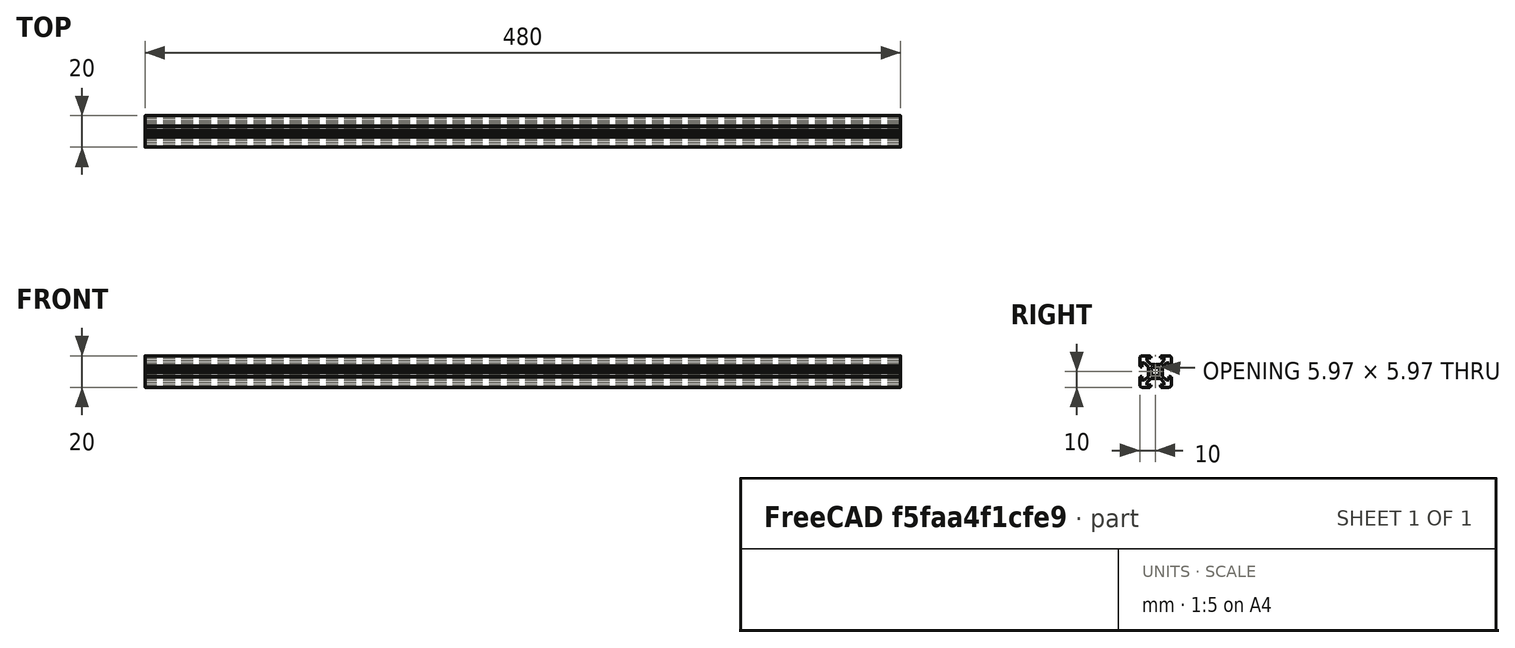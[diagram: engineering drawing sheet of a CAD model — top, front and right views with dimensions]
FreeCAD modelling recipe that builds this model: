
FCSTD DOCUMENT  (FreeCAD 0.19R)
Label: Tslot48
License: All rights reserved
LicenseURL: http://en.wikipedia.org/wiki/All_rights_reserved
objects: Sketcher::SketchObject×1, PartDesign::Pad×1, PartDesign::Body×1
note: 4 computed .brp shape members not serialized (recipe doc carries the construction recipe); baked Part::Feature solids carry a one-line shape summary decoded from their .brp

FEATURE [Sketcher::SketchObject] Sketch  label="T-Slot-Skizze"
  FullyConstrained = true
  MapMode = 5
  Placement = pos=(0,0,0) rot=(0.57735,0.57735,0.57735;2.0944rad)
  Support = -> [YZ_Plane]
  sketch-geometry (98):
    g0: LineSegment StartX=0 StartY=4.1 StartZ=0 EndX=0.65 EndY=4.5 EndZ=0
    g1: LineSegment StartX=0.65 StartY=4.5 StartZ=0 EndX=3 EndY=4.5 EndZ=0
    g2: LineSegment StartX=3 StartY=4.5 StartZ=0 EndX=5.5 EndY=7 EndZ=0
    g3: LineSegment StartX=5.5 StartY=7 StartZ=0 EndX=5.5 EndY=8.5 EndZ=0
    g4: LineSegment StartX=5.5 StartY=8.5 StartZ=0 EndX=3 EndY=8.5 EndZ=0
    g5: LineSegment StartX=3 StartY=8.5 StartZ=0 EndX=3 EndY=9.5 EndZ=0
    g6: LineSegment StartX=3 StartY=9.5 StartZ=0 EndX=3.5 EndY=9.5 EndZ=0
    g7: LineSegment StartX=3.5 StartY=9.5 StartZ=0 EndX=3.5 EndY=10 EndZ=0
    g8: LineSegment StartX=3.5 StartY=10 StartZ=0 EndX=8.5 EndY=10 EndZ=0
    g9: LineSegment StartX=10 StartY=8.5 StartZ=0 EndX=10 EndY=3.5 EndZ=0
    g10: LineSegment StartX=10 StartY=3.5 StartZ=0 EndX=9.5 EndY=3.5 EndZ=0
    g11: LineSegment StartX=9.5 StartY=3.5 StartZ=0 EndX=9.5 EndY=3 EndZ=0
    g12: LineSegment StartX=9.5 StartY=3 StartZ=0 EndX=8.5 EndY=3 EndZ=0
    g13: LineSegment StartX=8.5 StartY=3 StartZ=0 EndX=8.5 EndY=5.5 EndZ=0
    g14: LineSegment StartX=8.5 StartY=5.5 StartZ=0 EndX=7 EndY=5.5 EndZ=0
    g15: LineSegment StartX=7 StartY=5.5 StartZ=0 EndX=4.5 EndY=3 EndZ=0
    g16: LineSegment StartX=4.5 StartY=3 StartZ=0 EndX=4.5 EndY=0.65 EndZ=0
    g17: LineSegment StartX=4.5 StartY=0.65 StartZ=0 EndX=4.1 EndY=0 EndZ=0
    g18: ArcOfCircle CenterX=8.5 CenterY=8.5 CenterZ=0 NormalX=0 NormalY=0 NormalZ=1 AngleXU=0 Radius=1.5 StartAngle=0 EndAngle=1.5708
    g19: LineSegment StartX=0 StartY=-4.1 StartZ=0 EndX=0.65 EndY=-4.5 EndZ=0
    g20: LineSegment StartX=0.65 StartY=-4.5 StartZ=0 EndX=3 EndY=-4.5 EndZ=0
    g21: LineSegment StartX=3 StartY=-4.5 StartZ=0 EndX=5.5 EndY=-7 EndZ=0
    g22: LineSegment StartX=5.5 StartY=-7 StartZ=0 EndX=5.5 EndY=-8.5 EndZ=0
    g23: LineSegment StartX=5.5 StartY=-8.5 StartZ=0 EndX=3 EndY=-8.5 EndZ=0
    g24: LineSegment StartX=3 StartY=-8.5 StartZ=0 EndX=3 EndY=-9.5 EndZ=0
    g25: LineSegment StartX=3 StartY=-9.5 StartZ=0 EndX=3.5 EndY=-9.5 EndZ=0
    g26: LineSegment StartX=3.5 StartY=-9.5 StartZ=0 EndX=3.5 EndY=-10 EndZ=0
    g27: LineSegment StartX=3.5 StartY=-10 StartZ=0 EndX=8.5 EndY=-10 EndZ=0
    g28: LineSegment StartX=10 StartY=-8.5 StartZ=0 EndX=10 EndY=-3.5 EndZ=0
    g29: LineSegment StartX=10 StartY=-3.5 StartZ=0 EndX=9.5 EndY=-3.5 EndZ=0
    g30: LineSegment StartX=9.5 StartY=-3.5 StartZ=0 EndX=9.5 EndY=-3 EndZ=0
    g31: LineSegment StartX=9.5 StartY=-3 StartZ=0 EndX=8.5 EndY=-3 EndZ=0
    g32: LineSegment StartX=8.5 StartY=-3 StartZ=0 EndX=8.5 EndY=-5.5 EndZ=0
    g33: LineSegment StartX=8.5 StartY=-5.5 StartZ=0 EndX=7 EndY=-5.5 EndZ=0
    g34: LineSegment StartX=7 StartY=-5.5 StartZ=0 EndX=4.5 EndY=-3 EndZ=0
    g35: LineSegment StartX=4.5 StartY=-3 StartZ=0 EndX=4.5 EndY=-0.65 EndZ=0
    g36: ArcOfCircle CenterX=8.5 CenterY=-8.5 CenterZ=0 NormalX=0 NormalY=0 NormalZ=1 AngleXU=0 Radius=1.5 StartAngle=4.71239 EndAngle=6.28319
    g37: LineSegment StartX=4.5 StartY=-0.65 StartZ=0 EndX=4.1 EndY=0 EndZ=0
    g38: LineSegment StartX=0 StartY=-4.1 StartZ=0 EndX=-0.65 EndY=-4.5 EndZ=0
    g39: LineSegment StartX=-0.65 StartY=-4.5 StartZ=0 EndX=-3 EndY=-4.5 EndZ=0
    g40: LineSegment StartX=-3 StartY=-4.5 StartZ=0 EndX=-5.5 EndY=-7 EndZ=0
    g41: LineSegment StartX=-5.5 StartY=-7 StartZ=0 EndX=-5.5 EndY=-8.5 EndZ=0
    g42: LineSegment StartX=-5.5 StartY=-8.5 StartZ=0 EndX=-3 EndY=-8.5 EndZ=0
    g43: LineSegment StartX=-3 StartY=-8.5 StartZ=0 EndX=-3 EndY=-9.5 EndZ=0
    g44: LineSegment StartX=-3 StartY=-9.5 StartZ=0 EndX=-3.5 EndY=-9.5 EndZ=0
    g45: LineSegment StartX=-3.5 StartY=-9.5 StartZ=0 EndX=-3.5 EndY=-10 EndZ=0
    g46: LineSegment StartX=-3.5 StartY=-10 StartZ=0 EndX=-8.5 EndY=-10 EndZ=0
    g47: LineSegment StartX=-10 StartY=-8.5 StartZ=0 EndX=-10 EndY=-3.5 EndZ=0
    g48: LineSegment StartX=-10 StartY=-3.5 StartZ=0 EndX=-9.5 EndY=-3.5 EndZ=0
    g49: LineSegment StartX=-9.5 StartY=-3.5 StartZ=0 EndX=-9.5 EndY=-3 EndZ=0
    g50: LineSegment StartX=-9.5 StartY=-3 StartZ=0 EndX=-8.5 EndY=-3 EndZ=0
    g51: LineSegment StartX=-8.5 StartY=-3 StartZ=0 EndX=-8.5 EndY=-5.5 EndZ=0
    g52: LineSegment StartX=-8.5 StartY=-5.5 StartZ=0 EndX=-7 EndY=-5.5 EndZ=0
    g53: LineSegment StartX=-7 StartY=-5.5 StartZ=0 EndX=-4.5 EndY=-3 EndZ=0
    g54: LineSegment StartX=-4.5 StartY=-3 StartZ=0 EndX=-4.5 EndY=-0.65 EndZ=0
    g55: ArcOfCircle CenterX=-8.5 CenterY=-8.5 CenterZ=0 NormalX=0 NormalY=0 NormalZ=1 AngleXU=0 Radius=1.5 StartAngle=3.14159 EndAngle=4.71239
    g56: LineSegment StartX=-4.5 StartY=-0.65 StartZ=0 EndX=-4.1 EndY=0 EndZ=0
    g57: LineSegment StartX=-0.65 StartY=4.5 StartZ=0 EndX=-3 EndY=4.5 EndZ=0
    g58: LineSegment StartX=-3 StartY=4.5 StartZ=0 EndX=-5.5 EndY=7 EndZ=0
    g59: LineSegment StartX=-5.5 StartY=7 StartZ=0 EndX=-5.5 EndY=8.5 EndZ=0
    g60: LineSegment StartX=-5.5 StartY=8.5 StartZ=0 EndX=-3 EndY=8.5 EndZ=0
    g61: LineSegment StartX=-3 StartY=8.5 StartZ=0 EndX=-3 EndY=9.5 EndZ=0
    g62: LineSegment StartX=-3 StartY=9.5 StartZ=0 EndX=-3.5 EndY=9.5 EndZ=0
    g63: LineSegment StartX=-3.5 StartY=9.5 StartZ=0 EndX=-3.5 EndY=10 EndZ=0
    g64: LineSegment StartX=-3.5 StartY=10 StartZ=0 EndX=-8.5 EndY=10 EndZ=0
    g65: LineSegment StartX=-10 StartY=8.5 StartZ=0 EndX=-10 EndY=3.5 EndZ=0
    g66: LineSegment StartX=-10 StartY=3.5 StartZ=0 EndX=-9.5 EndY=3.5 EndZ=0
    g67: LineSegment StartX=-9.5 StartY=3.5 StartZ=0 EndX=-9.5 EndY=3 EndZ=0
    g68: LineSegment StartX=-9.5 StartY=3 StartZ=0 EndX=-8.5 EndY=3 EndZ=0
    g69: LineSegment StartX=-8.5 StartY=3 StartZ=0 EndX=-8.5 EndY=5.5 EndZ=0
    g70: LineSegment StartX=-8.5 StartY=5.5 StartZ=0 EndX=-7 EndY=5.5 EndZ=0
    g71: LineSegment StartX=-7 StartY=5.5 StartZ=0 EndX=-4.5 EndY=3 EndZ=0
    g72: LineSegment StartX=-4.5 StartY=3 StartZ=0 EndX=-4.5 EndY=0.65 EndZ=0
    g73: ArcOfCircle CenterX=-8.5 CenterY=8.5 CenterZ=0 NormalX=0 NormalY=0 NormalZ=1 AngleXU=0 Radius=1.5 StartAngle=1.5708 EndAngle=3.14159
    g74: LineSegment StartX=-4.5 StartY=0.65 StartZ=0 EndX=-4.1 EndY=0 EndZ=0
    g75: LineSegment StartX=0 StartY=4.1 StartZ=0 EndX=-0.65 EndY=4.5 EndZ=0
    g76: Circle CenterX=0 CenterY=0 CenterZ=0 NormalX=0 NormalY=0 NormalZ=1 AngleXU=0 Radius=3.55
    g77: Circle CenterX=0 CenterY=0 CenterZ=0 NormalX=0 NormalY=0 NormalZ=1 AngleXU=0 Radius=2.75
    g78: LineSegment StartX=1.3405 StartY=2.40116 StartZ=0 EndX=1.92324 EndY=2.9839 EndZ=0
    g79: LineSegment StartX=1.92324 StartY=2.9839 StartZ=0 EndX=2.9839 EndY=1.92324 EndZ=0
    g80: LineSegment StartX=2.9839 StartY=1.92324 StartZ=0 EndX=2.40116 EndY=1.3405 EndZ=0
    g81: ArcOfCircle CenterX=0 CenterY=0 CenterZ=0 NormalX=0 NormalY=0 NormalZ=1 AngleXU=0 Radius=2.75 StartAngle=0 EndAngle=0.509172
    g82: ArcOfCircle CenterX=0 CenterY=0 CenterZ=0 NormalX=0 NormalY=0 NormalZ=1 AngleXU=0 Radius=2.75 StartAngle=1.06162 EndAngle=1.5708
    g83: LineSegment StartX=-1.3405 StartY=2.40116 StartZ=0 EndX=-1.92324 EndY=2.9839 EndZ=0
    g84: LineSegment StartX=-1.92324 StartY=2.9839 StartZ=0 EndX=-2.9839 EndY=1.92324 EndZ=0
    g85: LineSegment StartX=-2.9839 StartY=1.92324 StartZ=0 EndX=-2.40116 EndY=1.3405 EndZ=0
    g86: ArcOfCircle CenterX=-1.3e-15 CenterY=6e-16 CenterZ=0 NormalX=0 NormalY=0 NormalZ=1 AngleXU=0 Radius=2.75 StartAngle=2.63242 EndAngle=3.14159
    g87: ArcOfCircle CenterX=-1.3e-15 CenterY=6e-16 CenterZ=0 NormalX=0 NormalY=0 NormalZ=1 AngleXU=0 Radius=2.75 StartAngle=1.5708 EndAngle=2.07997
    g88: LineSegment StartX=-1.34051 StartY=-2.40115 StartZ=0 EndX=-1.92325 EndY=-2.98389 EndZ=0
    g89: LineSegment StartX=-1.92325 StartY=-2.98389 StartZ=0 EndX=-2.9839 EndY=-1.92323 EndZ=0
    g90: LineSegment StartX=-2.9839 StartY=-1.92323 StartZ=0 EndX=-2.40116 EndY=-1.34049 EndZ=0
    g91: ArcOfCircle CenterX=-3e-16 CenterY=2e-16 CenterZ=0 NormalX=0 NormalY=0 NormalZ=1 AngleXU=0 Radius=2.75 StartAngle=3.14159 EndAngle=3.65076
    g92: ArcOfCircle CenterX=-3e-16 CenterY=2e-16 CenterZ=0 NormalX=0 NormalY=0 NormalZ=1 AngleXU=0 Radius=2.75 StartAngle=4.20321 EndAngle=4.71239
    g93: LineSegment StartX=1.34051 StartY=-2.40115 StartZ=0 EndX=1.92325 EndY=-2.98389 EndZ=0
    g94: LineSegment StartX=1.92325 StartY=-2.98389 StartZ=0 EndX=2.9839 EndY=-1.92323 EndZ=0
    g95: LineSegment StartX=2.9839 StartY=-1.92323 StartZ=0 EndX=2.40116 EndY=-1.34049 EndZ=0
    g96: ArcOfCircle CenterX=3e-16 CenterY=2e-16 CenterZ=0 NormalX=0 NormalY=0 NormalZ=1 AngleXU=0 Radius=2.75 StartAngle=4.71239 EndAngle=5.22156
    g97: ArcOfCircle CenterX=3e-16 CenterY=2e-16 CenterZ=0 NormalX=0 NormalY=0 NormalZ=1 AngleXU=0 Radius=2.75 StartAngle=5.77402 EndAngle=6.28319
  constraints (291):
    c: PointOnObject(g0,g-2)
    c: Coincident(g0,g1)
    c: Horizontal(g1)
    c: Coincident(g1,g2)
    c: Coincident(g2,g3)
    c: Vertical(g3)
    c: Coincident(g3,g4)
    c: Horizontal(g4)
    c: Coincident(g4,g5)
    c: Vertical(g5)
    c: Coincident(g5,g6)
    c: Horizontal(g6)
    c: Coincident(g6,g7)
    c: Coincident(g7,g8)
    c: Horizontal(g8)
    c: Vertical(g7)
    c: DistanceX(g-1,g5) = 3
    c: DistanceY(g4,g7) = 1.5
    c: DistanceY(g0,g7) = 5.5
    c: DistanceY(g3,g3) = 1.5
    c: DistanceY(g4,g5) = 1
    c: DistanceX(g-1,g1) = 3
    c: DistanceX(g-1,g7) = 3.5
    c: DistanceX(g0,g0) = 0.65
    c: DistanceY(g0,g0) = 0.4
    c: DistanceX(g-1,g3) = 5.5
    c: Vertical(g9)
    c: Coincident(g9,g10)
    c: Coincident(g10,g11)
    c: Coincident(g11,g12)
    c: Coincident(g12,g13)
    c: Vertical(g13)
    c: Coincident(g13,g14)
    c: Horizontal(g14)
    c: Coincident(g14,g15)
    c: Coincident(g15,g16)
    c: Vertical(g16)
    c: Coincident(g16,g17)
    c: PointOnObject(g17,g-1)
    c: Horizontal(g10)
    c: Horizontal(g12)
    c: Vertical(g11)
    c: Equal(g17,g0)
    c: Equal(g1,g16)
    c: Equal(g15,g2)
    c: Equal(g3,g14)
    c: Equal(g13,g4)
    c: Equal(g12,g5)
    c: Parallel(g15,g2)
    c: Equal(g11,g6)
    c: Equal(g10,g7)
    c: Equal(g9,g8)
    c: Tangent(g8,g18) = 1.5708
    c: Tangent(g9,g18) = 1.5708
    c: Radius(g18) = 1.5
    c: DistanceY(g-1,g8) = 10
    c: DistanceX(g-1,g9) = 10
    c: Coincident(g19,g20)
    c: Horizontal(g20)
    c: Coincident(g20,g21)
    c: Coincident(g21,g22)
    c: Vertical(g22)
    c: Coincident(g22,g23)
    c: Horizontal(g23)
    c: Coincident(g23,g24)
    c: Vertical(g24)
    c: Coincident(g24,g25)
    c: Horizontal(g25)
    c: Coincident(g25,g26)
    c: Coincident(g26,g27)
    c: Horizontal(g27)
    c: Vertical(g26)
    c: Vertical(g28)
    c: Coincident(g28,g29)
    c: Coincident(g29,g30)
    c: Coincident(g30,g31)
    c: Coincident(g31,g32)
    c: Vertical(g32)
    c: Coincident(g32,g33)
    c: Horizontal(g33)
    c: Coincident(g33,g34)
    c: Coincident(g34,g35)
    c: Vertical(g35)
    c: Coincident(g35,g37)
    c: Horizontal(g29)
    c: Horizontal(g31)
    c: Vertical(g30)
    c: Equal(g37,g19)
    c: Equal(g20,g35)
    c: Equal(g34,g21)
    c: Equal(g22,g33)
    c: Equal(g32,g23)
    c: Equal(g31,g24)
    c: Parallel(g34,g21)
    c: Equal(g30,g25)
    c: Equal(g29,g26)
    c: Equal(g28,g27)
    c: Tangent(g27,g36) = -1.5708
    c: Tangent(g28,g36) = -1.5708
    c: Radius(g36) = 1.5
    c: Equal(g9,g28)
    c: Equal(g12,g31)
    c: DistanceX(g-1,g28) = 10
    c: DistanceY(g27,g-1) = 10
    c: DistanceY(g30,g-1) = 3
    c: Equal(g33,g14)
    c: Equal(g35,g16)
    c: Equal(g17,g37)
    c: Coincident(g37,g17)
    c: Equal(g15,g34)
    c: PointOnObject(g19,g-2)
    c: DistanceY(g34,g-1) = 3
    c: DistanceX(g-1,g20) = 3
    c: Coincident(g38,g39)
    c: Horizontal(g39)
    c: Coincident(g39,g40)
    c: Coincident(g40,g41)
    c: Vertical(g41)
    c: Coincident(g41,g42)
    c: Horizontal(g42)
    c: Coincident(g42,g43)
    c: Vertical(g43)
    c: Coincident(g43,g44)
    c: Horizontal(g44)
    c: Coincident(g44,g45)
    c: Coincident(g45,g46)
    c: Horizontal(g46)
    c: Vertical(g45)
    c: Vertical(g47)
    c: Coincident(g47,g48)
    c: Coincident(g48,g49)
    c: Coincident(g49,g50)
    c: Coincident(g50,g51)
    c: Vertical(g51)
    c: Coincident(g51,g52)
    c: Horizontal(g52)
    c: Coincident(g52,g53)
    c: Coincident(g53,g54)
    c: Vertical(g54)
    c: Coincident(g54,g56)
    c: Horizontal(g48)
    c: Horizontal(g50)
    c: Vertical(g49)
    c: Equal(g39,g54)
    c: Equal(g53,g40)
    c: Equal(g41,g52)
    c: Equal(g51,g42)
    c: Equal(g50,g43)
    c: Parallel(g53,g40)
    c: Equal(g49,g44)
    c: Equal(g48,g45)
    c: Equal(g47,g46)
    c: Tangent(g46,g55) = 1.5708
    c: Tangent(g47,g55) = 1.5708
    c: Radius(g55) = 1.5
    c: Coincident(g38,g19)
    c: DistanceX(g39,g-1) = 3
    c: DistanceX(g38,g19) = 0.65
    c: DistanceY(g38,g19) = 0.4
    c: PointOnObject(g56,g-1)
    c: Equal(g56,g38)
    c: DistanceY(g53,g-1) = 3
    c: Equal(g22,g41)
    c: Equal(g42,g23)
    c: Equal(g24,g43)
    c: Equal(g25,g44)
    c: Equal(g26,g45)
    c: DistanceY(g46,g-1) = 10
    c: DistanceX(g47,g-1) = 10
    c: Coincident(g75,g57)
    c: Horizontal(g57)
    c: Coincident(g57,g58)
    c: Coincident(g58,g59)
    c: Vertical(g59)
    c: Coincident(g59,g60)
    c: Horizontal(g60)
    c: Coincident(g60,g61)
    c: Vertical(g61)
    c: Coincident(g61,g62)
    c: Horizontal(g62)
    c: Coincident(g62,g63)
    c: Coincident(g63,g64)
    c: Horizontal(g64)
    c: Vertical(g63)
    c: Vertical(g65)
    c: Coincident(g65,g66)
    c: Coincident(g66,g67)
    c: Coincident(g67,g68)
    c: Coincident(g68,g69)
    c: Vertical(g69)
    c: Coincident(g69,g70)
    c: Horizontal(g70)
    c: Coincident(g70,g71)
    c: Coincident(g71,g72)
    c: Vertical(g72)
    c: Coincident(g72,g74)
    c: Horizontal(g66)
    c: Horizontal(g68)
    c: Vertical(g67)
    c: Equal(g57,g72)
    c: Equal(g71,g58)
    c: Equal(g59,g70)
    c: Equal(g69,g60)
    c: Equal(g68,g61)
    c: Parallel(g71,g58)
    c: Equal(g67,g62)
    c: Equal(g66,g63)
    c: Equal(g65,g64)
    c: Tangent(g64,g73) = -1.5708
    c: Tangent(g65,g73) = -1.5708
    c: Radius(g73) = 1.5
    c: Equal(g74,g75)
    c: Coincident(g56,g74)
    c: Coincident(g0,g75)
    c: Equal(g0,g75)
    c: Equal(g1,g57)
    c: Equal(g2,g58)
    c: Equal(g3,g59)
    c: Equal(g4,g60)
    c: Equal(g5,g61)
    c: Equal(g6,g62)
    c: Equal(g7,g63)
    c: Equal(g8,g64)
    c: DistanceX(g65,g-1) = 10
    c: Coincident(g76,g-1)
    c: Coincident(g77,g-1)
    c: Radius(g76) = 3.55
    c: Radius(g77) = 2.75
    c: PointOnObject(g78,g77)
    c: PointOnObject(g78,g76)
    c: Coincident(g78,g79)
    c: PointOnObject(g79,g76)
    c: Coincident(g79,g80)
    c: PointOnObject(g80,g77)
    c: Coincident(g81,g-1)
    c: Coincident(g81,g80)
    c: Coincident(g82,g81)
    c: Coincident(g82,g78)
    c: Parallel(g78,g80)
    c: Parallel(g78,g2)
    c: Distance(g79) = 1.5
    c: Distance(g78,g80) = 1.5
    c: PointOnObject(g82,g-2)
    c: PointOnObject(g81,g-1)
    c: Coincident(g83,g84)
    c: Coincident(g84,g85)
    c: Coincident(g86,g85)
    c: Coincident(g87,g86)
    c: Coincident(g87,g83)
    c: Parallel(g83,g85)
    c: Distance(g84) = 1.5
    c: Distance(g83,g85) = 1.5
    c: Coincident(g82,g87)
    c: PointOnObject(g86,g-1)
    c: PointOnObject(g83,g76)
    c: PointOnObject(g83,g77)
    c: PointOnObject(g85,g77)
    c: PointOnObject(g84,g76)
    c: PointOnObject(g86,g77)
    c: Parallel(g85,g71)
    c: Coincident(g88,g89)
    c: Coincident(g89,g90)
    c: Coincident(g91,g90)
    c: Coincident(g92,g91)
    c: Coincident(g92,g88)
    c: Parallel(g88,g90)
    c: Distance(g89) = 1.5
    c: Distance(g88,g90) = 1.5
    c: PointOnObject(g88,g77)
    c: PointOnObject(g90,g77)
    c: Coincident(g86,g91)
    c: PointOnObject(g89,g76)
    c: PointOnObject(g88,g76)
    c: PointOnObject(g92,g-2)
    c: PointOnObject(g92,g77)
    c: Parallel(g88,g40)
    c: Coincident(g93,g94)
    c: Coincident(g94,g95)
    c: Coincident(g97,g95)
    c: Coincident(g96,g97)
    c: Coincident(g96,g93)
    c: Parallel(g93,g95)
    c: Distance(g94) = 1.5
    c: Distance(g93,g95) = 1.5
    c: Coincident(g81,g97)
    c: Coincident(g92,g96)
    c: PointOnObject(g93,g77)
    c: PointOnObject(g95,g77)
    c: PointOnObject(g94,g76)
    c: PointOnObject(g93,g76)
    c: Parallel(g93,g21)
FEATURE [PartDesign::Pad] Pad  label="T-Slot-Element"
  Direction = (1,1,1)
  Length = 480
  Length2 = 100
  Placement = pos=(0,0,0) rot=(0.57735,0.57735,0.57735;2.0944rad)
  Profile = -> Sketch
  Type = 0
FEATURE [PartDesign::Body] Body  label="T-Slot-Profil 20x20"
  Group = -> [Sketch,Pad]
  Origin = -> Origin
  Tip = -> Pad
